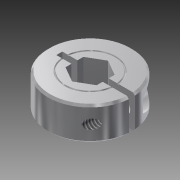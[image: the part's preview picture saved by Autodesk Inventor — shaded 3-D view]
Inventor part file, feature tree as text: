
AUTODESK INVENTOR PART (.ipt)
format: ipt  version: 2014 (Build 180170000, 170)  size: 416,256 bytes
history: native  units: mm
features: sketch x6, extrude x4, hole x2, other x2, surface_op x1, thread x1, projected_geometry x1
ambient origin geometry x8: Origin, YZ Plane, XZ Plane, XY Plane, X Axis, Y Axis, Z Axis, Center Point
bodies: Solid1 (feature_tree)
feature tree (17):
  surface_op  "Stitch Surface1"
  thread  "Thread1"  [1 undecoded]
  hole  "Hole1"  [1 undecoded]
  extrude  "Extrusion1"  Depth=10.0mm TaperAngle=0.0deg
  hole  "Hole2"  [1 undecoded]
  extrude  "Extrusion2"  [1 undecoded]
  extrude  "Extrusion3"  [1 undecoded]
  extrude  "Extrusion4"  [1 undecoded]
  sketch  "Sketch1"  dims[d2=3.797mm d3=6.0mm d4=12.7mm d5=2.362mm d6=14.3117mm d7=8.0mm d8=20.594885mm d9=9.25mm d10=0.0mm]
  sketch  "Sketch2"  dims[d11=2.642mm d12=10.0mm d13=12.7mm d14=2.362mm d15=14.3117mm d16=8.0mm d17=20.594885mm d18=8.5mm d19=0.0mm]
  sketch  "Sketch3"  dims[d20=9.525mm d21=10.0mm d22=0.0mm]
  projected_geometry  "Projected Loop1"
  sketch  "Sketch4"  dims[d23=10.0mm d24=0.0mm]
  sketch  "Sketch5"
  sketch  "Sketch6"
  other  "Composite1"
  other  "Srf1"
note: 6 required parameter values undecoded (feature->parameter linkage not recoverable at this tier; creation-order binding heuristic only, values carry confidence <= 0.55)
